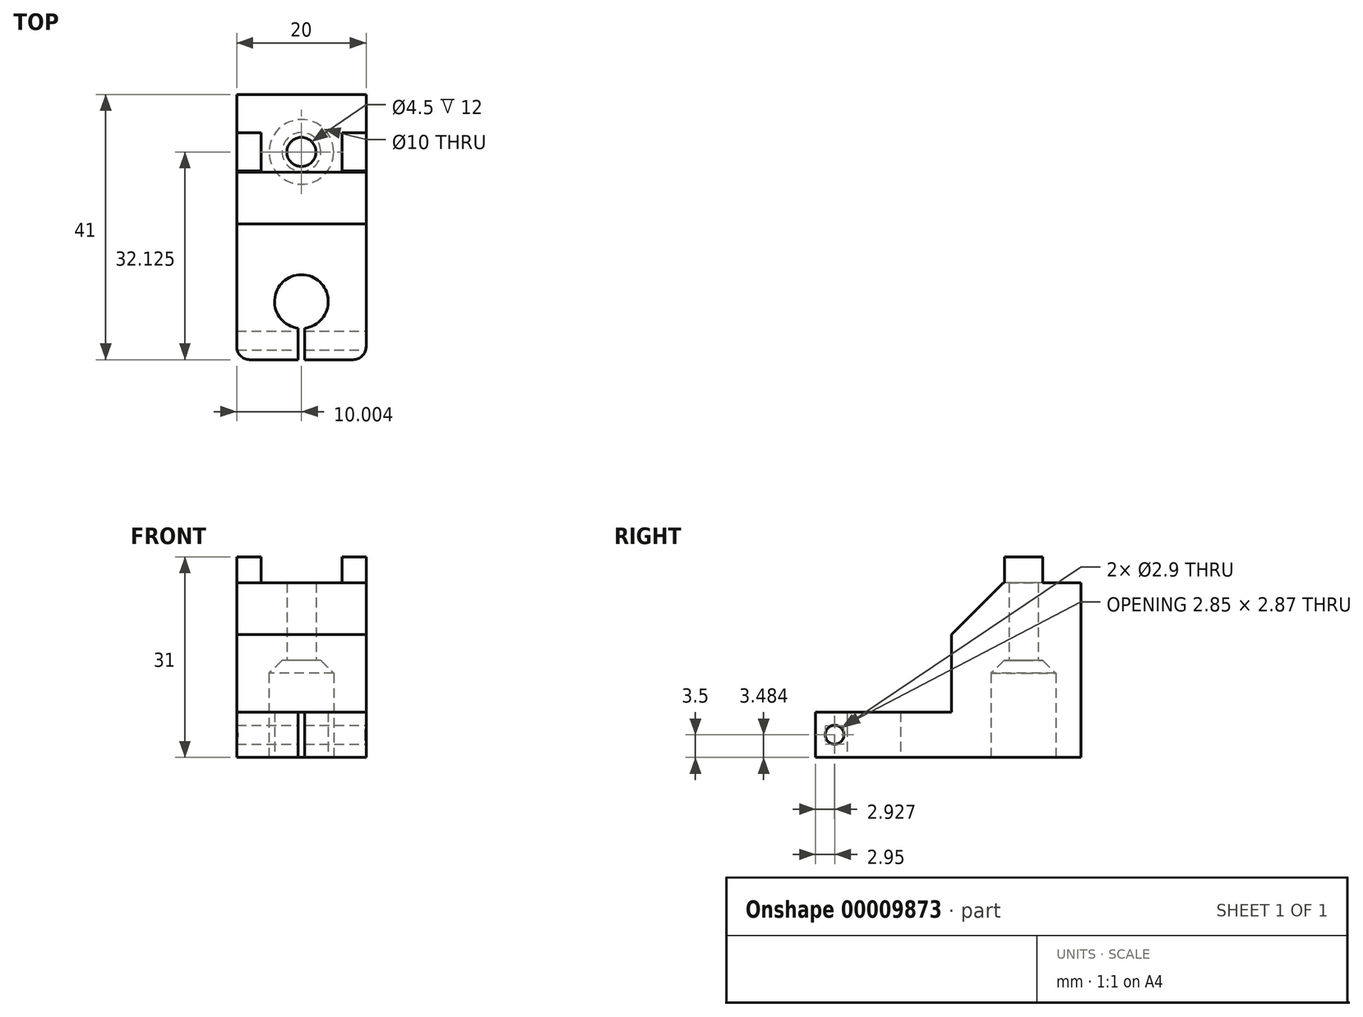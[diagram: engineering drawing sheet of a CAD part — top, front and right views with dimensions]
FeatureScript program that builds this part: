
annotation { "Feature Type Name" : "Feature", "Feature Type Description" : "" }
export const myFeature = defineFeature(function(context is Context, id is Id, definition is map)
    precondition{}
    {
        {
            var Q0;
            Q0=qCreatedBy(makeId("Top.planeOp"),FACE);
            var sketch = newSketch(context, id + "F0", { "sketchPlane" : qUnion([Q0])});
            skLineSegment(sketch, "E0.bottom", {"start": v(-6.6, 0) * mm, "end": v(13.4, 0) * mm});
            skLineSegment(sketch, "E0.top", {"start": v(-6.6, 41) * mm, "end": v(13.4, 41) * mm});
            skLineSegment(sketch, "E0.left", {"start": v(-6.6, 0) * mm, "end": v(-6.6, 41) * mm});
            skLineSegment(sketch, "E0.right", {"start": v(13.4, 0) * mm, "end": v(13.4, 41) * mm});
            skLineSegment(sketch, "E1", {"start": v(-6.6, 21) * mm, "end": v(13.4, 21) * mm, "construction": true});
            skPoint(sketch, "E2.centerSnap0", {"position": v(3.4, 41) * mm});
            skCircle(sketch, "E3", {"center": v(3.4, 9) * mm, "radius": 4.15 * mm});
            skLineSegment(sketch, "E4.bottom", {"start": v(3.9, 0) * mm, "end": v(2.9, 0) * mm});
            skLineSegment(sketch, "E4.top", {"start": v(3.9, 9) * mm, "end": v(2.9, 9) * mm});
            skLineSegment(sketch, "E4.left", {"start": v(3.9, 0) * mm, "end": v(3.9, 9) * mm});
            skLineSegment(sketch, "E4.right", {"start": v(2.9, 0) * mm, "end": v(2.9, 9) * mm});
            skLineSegment(sketch, "E5.bottom", {"start": v(1.15, 32.12) * mm, "end": v(5.65, 32.12) * mm});
            skArc(sketch, "E6", {"start": v(5.65, 32.12) * mm, "mid": v(3.4, 34.38) * mm, "end": v(1.15, 32.12) * mm});
            skLineSegment(sketch, "E7", {"start": v(3.4, 21) * mm, "end": v(3.4, 29.88) * mm});
            skLineSegment(sketch, "E8", {"start": v(3.4, 32.12) * mm, "end": v(3.4, 41) * mm});
            skCircle(sketch, "E9", {"center": v(3.4, 9) * mm, "radius": 7.75 * mm});
            skLineSegment(sketch, "E10", {"start": v(-6.6, 21) * mm, "end": v(13.4, 21) * mm});
            skArc(sketch, "E11", {"start": v(1.15, 32.12) * mm, "mid": v(3.4, 29.88) * mm, "end": v(5.65, 32.12) * mm});
            skLineSegment(sketch, "E12.bottom", {"start": v(-6.6, 35.08) * mm, "end": v(-2.85, 35.08) * mm});
            skLineSegment(sketch, "E12.top", {"start": v(-6.6, 29.18) * mm, "end": v(-2.85, 29.18) * mm});
            skLineSegment(sketch, "E12.left", {"start": v(-6.6, 35.08) * mm, "end": v(-6.6, 29.18) * mm});
            skLineSegment(sketch, "E12.right", {"start": v(-2.85, 35.07) * mm, "end": v(-2.85, 29.17) * mm});
            skLineSegment(sketch, "E13.bottom", {"start": v(13.4, 35.08) * mm, "end": v(9.65, 35.08) * mm});
            skLineSegment(sketch, "E13.top", {"start": v(13.4, 29.18) * mm, "end": v(9.65, 29.18) * mm});
            skLineSegment(sketch, "E13.left", {"start": v(13.4, 35.08) * mm, "end": v(13.4, 29.17) * mm});
            skLineSegment(sketch, "E13.right", {"start": v(9.65, 35.07) * mm, "end": v(9.65, 29.17) * mm});
            skPoint(sketch, "E14", {"position": v(-2.85, 32.12) * mm});
            skCircle(sketch, "E15", {"center": v(3.4, 32.12) * mm, "radius": 5 * mm});
            skSolve(sketch);
        }
        {
            var Q0;
            Q0=makeQuery(id+"F0.imprint","IMPRINT",FACE,{"disambiguationData":[TD([[makeQuery(id+"F0.imprint","IMPRINT",EDGE,{"derivedFrom":sQuery(id+"F0.wireOp",EDGE,"E0.top")}),-1.0]])]});
            var Q1;
            {var subQ1=sQuery(id+"F0.wireOp",EDGE,"E0.bottom");var subQ5=sQuery(id+"F0.wireOp",EDGE,"E0.left");var subQ6=makeQuery(id+"F0.imprint","INTERSECT",VERTEX,{"derivedFrom":[subQ1,subQ5]});Q1=makeQuery(id+"F0.imprint","IMPRINT",FACE,{"disambiguationData":[TD([[makeQuery(id+"F0.imprint","IMPRINT",EDGE,{"disambiguationData":[TD([[subQ6,-1.0]])],"derivedFrom":subQ5}),-1.0]])]});}
            var Q2;
            {var subQ0=sQuery(id+"F0.wireOp",EDGE,"E4.left");var subQ1=sQuery(id+"F0.wireOp",EDGE,"E3");var subQ2=makeQuery(id+"F0.imprint","INTERSECT",VERTEX,{"derivedFrom":[subQ1,subQ0]});Q2=makeQuery(id+"F0.imprint","IMPRINT",FACE,{"disambiguationData":[TD([[makeQuery(id+"F0.imprint","IMPRINT",EDGE,{"disambiguationData":[TD([[subQ2,-1.0]])],"derivedFrom":subQ1}),-1.0]])]});}
            extrude(context, id + "F1", {"entities" : qUnion([Q0, Q1, Q2]), "depth" : 7 * mm});
        }
        {
            var Q0;
            Q0=makeQuery(id+"FQucasgnR9fUPlY_1.boolean.opBoolean","MERGE",FACE,{"derivedFrom":[makeQuery(id+"F1.opExtrude","SWEPT_FACE",FACE,{"disambiguationData":[OSD([sQuery(id+"F0.wireOp",EDGE,"E0.right")])]}),makeQuery(id+"FQucasgnR9fUPlY_1.opExtrude","SWEPT_FACE",FACE,{"disambiguationData":[OSD([sQuery(id+"Fag0aYCVP3Ujfj8_1.wireOp",EDGE,"1siYL01j-m5db-GpVy-yTCy-yeia6Dgr4sKR.left")])]})]});
            var sketch = newSketch(context, id + "F2", { "sketchPlane" : qUnion([Q0])});
            skCircle(sketch, "E16", {"center": v(2.95, 3.5) * mm, "radius": 1.45 * mm});
            skPoint(sketch, "E16.centerSnap0", {"position": v(0, 3.5) * mm});
            skSolve(sketch);
        }
        {
            var Q0;
            Q0=qSketchRegion(id+"F2",true);
            extrude(context, id + "F3", {"entities" : qUnion([Q0]), "operationType" : NewBodyOperationType.REMOVE, "oppositeDirection" : true, "depth" : 25 * mm});
        }
        {
            var Q0;
            Q0=makeQuery(id+"F1.opExtrude","SWEPT_EDGE",EDGE,{"disambiguationData":[OSD([sQuery(id+"F0.wireOp",EDGE,"E0.bottom"),sQuery(id+"F0.wireOp",EDGE,"E0.right")])]});
            var Q1;
            Q1=makeQuery(id+"F1.opExtrude","SWEPT_EDGE",EDGE,{"disambiguationData":[OSD([sQuery(id+"F0.wireOp",EDGE,"E0.bottom"),sQuery(id+"F0.wireOp",EDGE,"E0.left")])]});
            var Q2;
            Q2=makeQuery(id+"F1.opExtrude","SWEPT_EDGE",EDGE,{"disambiguationData":[OSD([sQuery(id+"F0.wireOp",EDGE,"E0.top"),sQuery(id+"F0.wireOp",EDGE,"E0.right")])]});
            var Q3;
            Q3=makeQuery(id+"F1.opExtrude","SWEPT_EDGE",EDGE,{"disambiguationData":[OSD([sQuery(id+"F0.wireOp",EDGE,"E0.top"),sQuery(id+"F0.wireOp",EDGE,"E0.left")])]});
            var Q4;
            Q4=makeQuery(id+"FxEKCNikidz0gRl_1.opExtrude","SWEPT_EDGE",EDGE,{"disambiguationData":[OSD([sQuery(id+"F0.wireOp",EDGE,"E0.left"),sQuery(id+"F0.wireOp",EDGE,"E10")])]});
            var Q5;
            Q5=makeQuery(id+"FxEKCNikidz0gRl_1.opExtrude","SWEPT_EDGE",EDGE,{"disambiguationData":[OSD([sQuery(id+"F0.wireOp",EDGE,"E0.right"),sQuery(id+"F0.wireOp",EDGE,"E10")])]});
            fillet(context, id + "F4", {"entities" : qUnion([Q0, Q1, Q2, Q3, Q4, Q5]), "radius" : 2 * mm, "tangentPropagation" : true, "allowEdgeOverflow" : false});
        }
        {
            var Q0;
            {var subQ0=sQuery(id+"F0.wireOp",EDGE,"E7");Q0=makeQuery(id+"F0.imprint","IMPRINT",FACE,{"disambiguationData":[TD([[makeQuery(id+"F0.imprint","IMPRINT",EDGE,{"derivedFrom":subQ0}),-1.0]])]});}
            var Q1;
            {var subQ0=sQuery(id+"F0.wireOp",EDGE,"E7");Q1=makeQuery(id+"F0.imprint","IMPRINT",FACE,{"disambiguationData":[TD([[makeQuery(id+"F0.imprint","IMPRINT",EDGE,{"derivedFrom":subQ0}),1.0]])]});}
            var Q2;
            {var subQ11=sQuery(id+"F0.wireOp",EDGE,"E13.bottom");Q2=makeQuery(id+"F0.imprint","IMPRINT",FACE,{"disambiguationData":[TD([[makeQuery(id+"F0.imprint","IMPRINT",EDGE,{"derivedFrom":subQ11}),-1.0]])]});}
            var Q3;
            {var subQ9=sQuery(id+"F0.wireOp",EDGE,"E12.bottom");Q3=makeQuery(id+"F0.imprint","IMPRINT",FACE,{"disambiguationData":[TD([[makeQuery(id+"F0.imprint","IMPRINT",EDGE,{"derivedFrom":subQ9}),1.0]])]});}
            extrude(context, id + "F5", {"entities" : qUnion([Q0, Q1, Q2, Q3]), "operationType" : NewBodyOperationType.ADD, "depth" : 27 * mm});
        }
        {
            var Q0;
            Q0=makeQuery(id+"F0.imprint","IMPRINT",FACE,{"disambiguationData":[TD([[makeQuery(id+"F0.imprint","IMPRINT",EDGE,{"derivedFrom":sQuery(id+"F0.wireOp",EDGE,"E12.bottom")}),-1.0]])]});
            var Q1;
            Q1=makeQuery(id+"F0.imprint","IMPRINT",FACE,{"disambiguationData":[TD([[makeQuery(id+"F0.imprint","IMPRINT",EDGE,{"derivedFrom":sQuery(id+"F0.wireOp",EDGE,"E13.bottom")}),1.0]])]});
            extrude(context, id + "F6", {"entities" : qUnion([Q0, Q1]), "operationType" : NewBodyOperationType.ADD, "depth" : 31 * mm});
        }
        {
            var Q0;
            Q0=makeQuery(id+"F5.opExtrude","CAP_EDGE",EDGE,{"disambiguationData":[OSD([sQuery(id+"F0.wireOp",EDGE,"E10")])],"isStart":false});
            chamfer(context, id + "F7", {"entities" : qUnion([Q0]), "width" : 8 * mm, "tangentPropagation" : true});
        }
        {
            var Q0;
            {var subQ5=sQuery(id+"F0.wireOp",EDGE,"E11");var subQ6=sQuery(id+"F0.wireOp",EDGE,"E7");var subQ7=makeQuery(id+"F0.imprint","INTERSECT",VERTEX,{"derivedFrom":[subQ6,subQ5]});Q0=makeQuery(id+"F0.imprint","IMPRINT",FACE,{"disambiguationData":[TD([[makeQuery(id+"F0.imprint","IMPRINT",EDGE,{"disambiguationData":[TD([[subQ7,1.0]])],"derivedFrom":subQ6}),1.0]])]});}
            var Q1;
            {var subQ5=sQuery(id+"F0.wireOp",EDGE,"E11");var subQ6=sQuery(id+"F0.wireOp",EDGE,"E7");var subQ7=makeQuery(id+"F0.imprint","INTERSECT",VERTEX,{"derivedFrom":[subQ6,subQ5]});Q1=makeQuery(id+"F0.imprint","IMPRINT",FACE,{"disambiguationData":[TD([[makeQuery(id+"F0.imprint","IMPRINT",EDGE,{"disambiguationData":[TD([[subQ7,1.0]])],"derivedFrom":subQ6}),-1.0]])]});}
            extrude(context, id + "F8", {"entities" : qUnion([Q0, Q1]), "operationType" : NewBodyOperationType.REMOVE, "depth" : 15 * mm});
        }
        {
            var Q0;
            Q0=makeQuery(id+"F8.boolean.opBoolean","COPY",EDGE,{"derivedFrom":makeQuery(id+"F8.opExtrude","CAP_EDGE",EDGE,{"disambiguationData":[OSD([sQuery(id+"F0.wireOp",EDGE,"E15")])],"isStart":false})});
            chamfer(context, id + "F9", {"entities" : qUnion([Q0]), "width" : 2 * mm, "tangentPropagation" : true});
        }
    });
